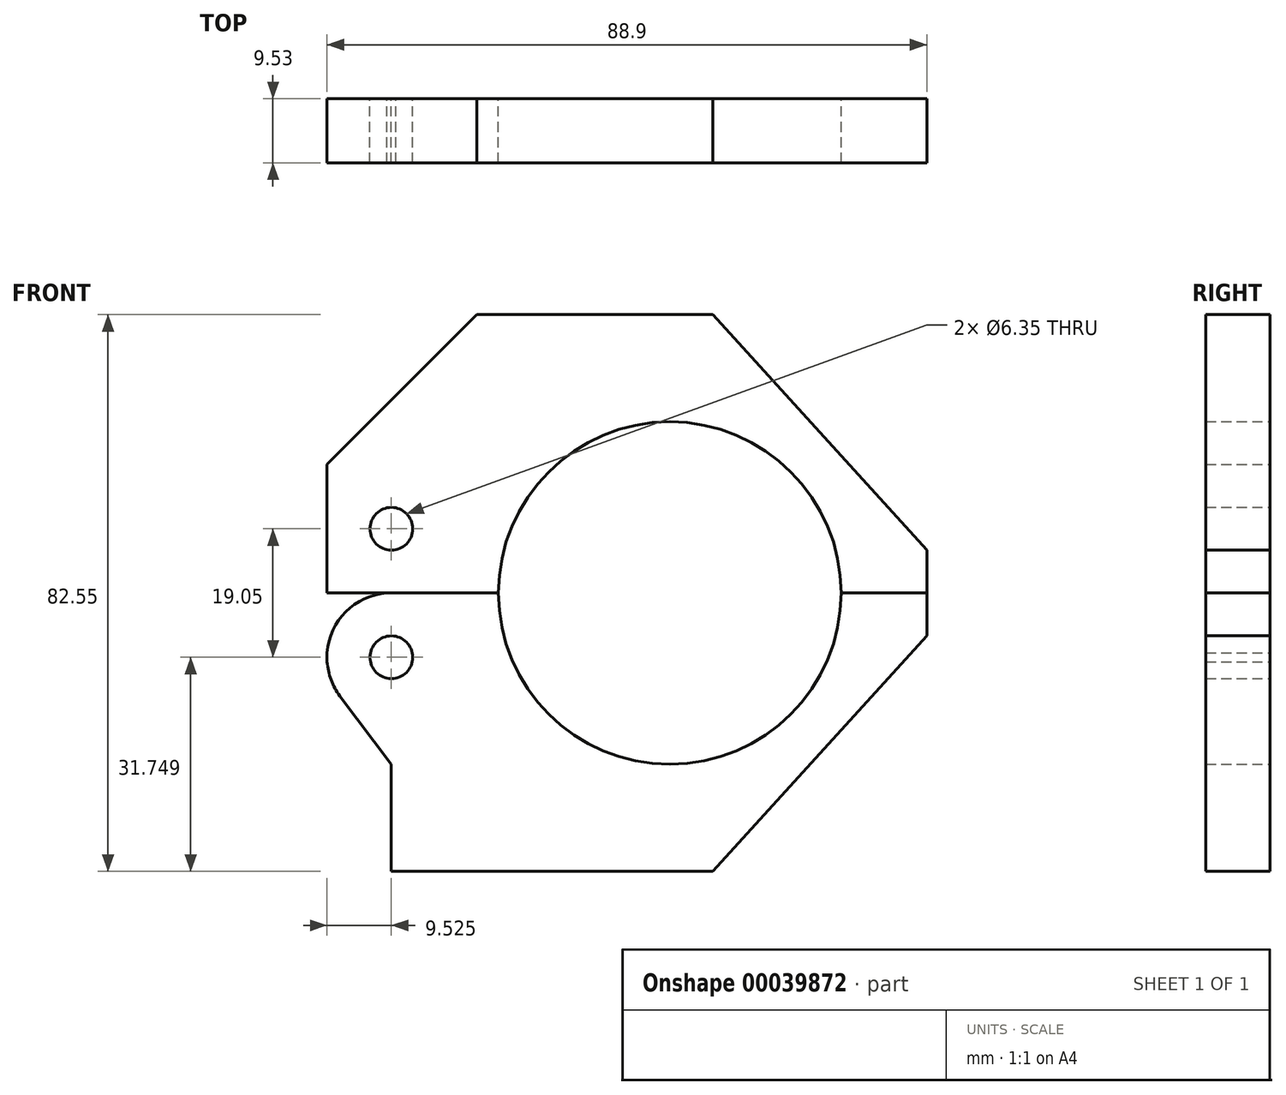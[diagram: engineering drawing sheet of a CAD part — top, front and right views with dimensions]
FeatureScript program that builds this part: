
annotation { "Feature Type Name" : "Feature", "Feature Type Description" : "" }
export const myFeature = defineFeature(function(context is Context, id is Id, definition is map)
    precondition{}
    {
        {
            var Q0;
            Q0=qCreatedBy(makeId("Front.planeOp"),FACE);
            var sketch = newSketch(context, id + "F0", { "sketchPlane" : qUnion([Q0])});
            skLineSegment(sketch, "E0.bottom", {"start": v(-28.58, 54.32) * mm, "end": v(6.35, 54.32) * mm});
            skLineSegment(sketch, "E0.top", {"start": v(-50.8, -28.23) * mm, "end": v(6.35, -28.23) * mm});
            skLineSegment(sketch, "E0.left", {"start": v(-50.8, 32.1) * mm, "end": v(-50.8, 2.86) * mm});
            skLineSegment(sketch, "E0.right", {"start": v(38.1, 19.4) * mm, "end": v(38.1, 6.7) * mm});
            skLineSegment(sketch, "E1", {"start": v(-50.8, 13.04) * mm, "end": v(38.1, 13.04) * mm});
            skCircle(sketch, "E2", {"center": v(0, 13.04) * mm, "radius": 25.4 * mm});
            skLineSegment(sketch, "E3", {"start": v(38.1, 19.4) * mm, "end": v(6.35, 54.32) * mm});
            skLineSegment(sketch, "E4.MirrorCS", {"start": v(38.1, 6.7) * mm, "end": v(6.35, -28.23) * mm});
            skLineSegment(sketch, "E5", {"start": v(-50.8, 32.1) * mm, "end": v(-28.58, 54.32) * mm});
            skCircle(sketch, "E6", {"center": v(-41.28, 22.57) * mm, "radius": 3.18 * mm});
            skCircle(sketch, "E7.MirrorC", {"center": v(-41.28, 3.52) * mm, "radius": 3.18 * mm});
            skLineSegment(sketch, "E8", {"start": v(-41.27, -28.23) * mm, "end": v(-41.27, -12.36) * mm});
            skArc(sketch, "E9", {"start": v(-40.62, 13.04) * mm, "mid": v(-49.67, 8.07) * mm, "end": v(-48.9, -2.22) * mm});
            skLineSegment(sketch, "E10", {"start": v(-41.27, -12.36) * mm, "end": v(-48.9, -2.22) * mm});
            skPoint(sketch, "E11.orphan", {"position": v(38.1, 54.32) * mm});
            skPoint(sketch, "E12.orphan", {"position": v(38.1, -28.23) * mm});
            skPoint(sketch, "E13.orphan", {"position": v(-50.8, 54.32) * mm});
            skSolve(sketch);
        }
        {
            var Q0;
            Q0=makeQuery(id+"F0.imprint","IMPRINT",FACE,{"disambiguationData":[TD([[makeQuery(id+"F0.imprint","IMPRINT",EDGE,{"derivedFrom":sQuery(id+"F0.wireOp",EDGE,"E0.bottom")}),-1.0]])]});
            extrude(context, id + "F1", {"entities" : qUnion([Q0]), "depth" : 9.52 * mm});
        }
        {
            var Q0;
            {var subQ9=sQuery(id+"F0.wireOp",EDGE,"E4.MirrorCS");Q0=makeQuery(id+"F0.imprint","IMPRINT",FACE,{"disambiguationData":[TD([[makeQuery(id+"F0.imprint","IMPRINT",EDGE,{"derivedFrom":subQ9}),-1.0]])]});}
            extrude(context, id + "F2", {"entities" : qUnion([Q0]), "depth" : 9.52 * mm});
        }
    });
